# Revit family: Building-IEC309Connections-GEWISS-44IB-INTERLOCKED-SOCKET-OUTLETS_IP44_WITHOUT_BOTTOM
name_source: partatom
category: Apparecchi elettrici
revit_build: Autodesk Revit 2016 (Build: 20161004_0715(x64)
units: mm (PartAtom-declared; Revit-internal decimal feet)

## family parameters
Condiviso = No
Host = Muro
Mantenere orientamento annotazione = Sì
Numero OmniClass = 23.80.50.14
Punto di calcolo locali = No
Quota connettore circolare = Usa diametro
Sempre verticale = Sì
Taglio con vuoti quando caricato = No
Tipo di parte = Normale
Titolo OmniClass = Plug Connectors

## types (22) — shared parameters
Altezza da terra = 820 mm
Carico apparente = 0 VA
Catalogue = BUILDING
Catalogue Range = 44 IB
Classificazione carico = Altro
Electrocod = 2220
Frequency = 50/60 Hz
Glow Wire Test = 850 °C (active parts) - 650 °C (passive parts)
Glow wire test: = 850 °C (active parts) - 650 °C (passive parts)
IDF = e04837b6-ddbd-45f3-abac-050fc58771e5
IDT = ec1a1901-e242-435b-8cd0-c029da0151fc
IP degree = IP44
Immagine tipo = GW66110.jpg
Numero poli = 3
Operating temperature: = -25 +40 °C
Potenza = 500 V
Presa = GEWISS - NERO
Produttore = GEWISS S.p.A.
Protection = NO (SBF)
Rated frequency (Hz) = 50/60 Hz
SEO = Socket outlet
Shock resistance = IK08
Struttura = GEWISS - Grigio RAL - 7035
Technical sheet = https://www.gewiss.com
Thermo-pressure with ball = 125
Tipo simbolo = PRESAIND : 3P
Typology = Horizontal
URL = https://www.gewiss.com
Version file RFA = 18.0
Vetro = GEWISS - vetro
With back-mounting box = No
Working temperature = -25 ÷ +40 °C

## per-type parameters (varying)
| type | Colour | Colour: | Descrizione | EAN code | Modello | No. of poles | Number of poles | Rated current (A) | Rated current (In) | Rated voltage | Reference h |
| GW66103 - 16A 3P+N+E 110V H.INT.SOCK.O.N.B. 4H SBF | Yellow | Yellow | 16A 3P+N+E 110V H.INT.SOCK.O.N.B. 4H SBF | 8011564029095 | GW66103 | 3P+N+E | 3P+N+E | 16 | 16 | 100-130V | 4 |
| GW66112 - 32A 2P+E 110V H.INT.SOCK.O.N.B. 4H SBF | Yellow | Yellow | 32A 2P+E 110V H.INT.SOCK.O.N.B. 4H SBF | 8011564029187 | GW66112 | 2P+E | 2P+E | 32 | 32 | 100-130V | 4 |
| GW66122 - 32A 3P+N+E 500V H.INT.SOCK.O.N.B. 7H SBF | Black | Black | 32A 3P+N+E 500V H.INT.SOCK.O.N.B. 7H SBF | 8011564029286 | GW66122 | 3P+N+E | 3P+N+E | 32 | 32 | 480-500V | 7 |
| GW66117 - 32A 3P+N+E 230V H.INT.SOCK.O.N.B. 9H SBF | Blue | Blue | 32A 3P+N+E 230V H.INT.SOCK.O.N.B. 9H SBF | 8011564029231 | GW66117 | 3P+N+E | 3P+N+E | 32 | 32 | 200-250V | 9 |
| GW66110 - 16A 3P+E 500V H.INT.SOCK.O.N.B. 7H SBF | Black | Black | 16A 3P+E 500V H.INT.SOCK.O.N.B. 7H SBF | 8011564029163 | GW66110 | 3P+E | 3P+E | 16 | 16 | 480-500V | 7 |
| GW66121 - 32A 3P+E 500V H.INT.SOCK.O.N.B. 7H SBF | Black | Black | 32A 3P+E 500V H.INT.SOCK.O.N.B. 7H SBF | 8011564029279 | GW66121 | 3P+E | 3P+E | 32 | 32 | 480-500V | 7 |
| GW66120 - 32A 3P+N+E 400V H.INT.SOCK.O.N.B. 6H SBF | Red | Red | 32A 3P+N+E 400V H.INT.SOCK.O.N.B. 6H SBF | 8011564029262 | GW66120 | 3P+N+E | 3P+N+E | 32 | 32 | 380-415V | 6 |
| GW66106 - 16A 3P+N+E 230V H.INT.SOCK.O.N.B. 9H SBF | Blue | Blue | 16A 3P+N+E 230V H.INT.SOCK.O.N.B. 9H SBF | 8011564029125 | GW66106 | 3P+N+E | 3P+N+E | 16 | 16 | 200-250V | 9 |
| GW66104 - 16A 2P+E 230V H.INT.SOCK.O.N.B. 6H SBF | Blue | Blue | 16A 2P+E 230V H.INT.SOCK.O.N.B. 6H SBF | 8011564029101 | GW66104 | 2P+E | 2P+E | 16 | 16 | 200-250V | 6 |
| GW66107 - 16A 2P+E 400V H.INT.SOCK.O.N.B. 9H SBF | Red | Red | 16A 2P+E 400V H.INT.SOCK.O.N.B. 9H SBF | 8011564029132 | GW66107 | 2P+E | 2P+E | 16 | 16 | 380-415V | 9 |
| GW66101 - 16A 2P+E 110V H.INT.SOCK.O.N.B. 4H SBF | Yellow | Yellow | 16A 2P+E 110V H.INT.SOCK.O.N.B. 4H SBF | 8011564029071 | GW66101 | 2P+E | 2P+E | 16 | 16 | 100-130V | 4 |
| GW66116 - 32A 3P+E 230V H.INT.SOCK.O.N.B. 9H SBF | Blue | Blue | 32A 3P+E 230V H.INT.SOCK.O.N.B. 9H SBF | 8011564029224 | GW66116 | 3P+E | 3P+E | 32 | 32 | 200-250V | 9 |
| GW66119 - 32A 3P+E 400V H.INT.SOCK.O.N.B. 6H SBF | Red | Red | 32A 3P+E 400V H.INT.SOCK.O.N.B. 6H SBF | 8011564029255 | GW66119 | 3P+E | 3P+E | 32 | 32 | 380-415V | 6 |
| GW66109 - 16A 3P+N+E 400V H.INT.SOCK.O.N.B. 6H SBF | Red | Red | 16A 3P+N+E 400V H.INT.SOCK.O.N.B. 6H SBF | 8011564029156 | GW66109 | 3P+N+E | 3P+N+E | 16 | 16 | 380-415V | 6 |
| GW66113 - 32A 3P+E 110V H.INT.SOCK.O.N.B. 4H SBF | Yellow | Yellow | 32A 3P+E 110V H.INT.SOCK.O.N.B. 4H SBF | 8011564029194 | GW66113 | 3P+E | 3P+E | 32 | 32 | 100-130V | 4 |
| GW66105 - 16A 3P+E 230V H.INT.SOCK.O.N.B. 9H SBF | Blue | Blue | 16A 3P+E 230V H.INT.SOCK.O.N.B. 9H SBF | 8011564029118 | GW66105 | 3P+E | 3P+E | 16 | 16 | 200-250V | 9 |
| GW66115 - 32A 2P+E 230V H.INT.SOCK.O.N.B. 6H SBF | Blue | Blue | 32A 2P+E 230V H.INT.SOCK.O.N.B. 6H SBF | 8011564029217 | GW66115 | 2P+E | 2P+E | 32 | 32 | 200-250V | 6 |
| GW66114 - 32A 3P+N+E 110V H.INT.SOCK.O.N.B. 4H SBF | Yellow | Yellow | 32A 3P+N+E 110V H.INT.SOCK.O.N.B. 4H SBF | 8011564029200 | GW66114 | 3P+N+E | 3P+N+E | 32 | 32 | 100-130V | 4 |
| GW66102 - 16A 3P+E 110V H.INT.SOCK.O.N.B. 4H SBF | Yellow | Yellow | 16A 3P+E 110V H.INT.SOCK.O.N.B. 4H SBF | 8011564029088 | GW66102 | 3P+E | 3P+E | 16 | 16 | 100-130V | 4 |
| GW66118 - 32A 2P+E 400V H.INT.SOCK.O.N.B. 9H SBF | Red | Red | 32A 2P+E 400V H.INT.SOCK.O.N.B. 9H SBF | 8011564029248 | GW66118 | 2P+E | 2P+E | 32 | 32 | 380-415V | 9 |
| GW66108 - 16A 3P+E 400V H.INT.SOCK.O.N.B. 6H SBF | Red | Red | 16A 3P+E 400V H.INT.SOCK.O.N.B. 6H SBF | 8011564029149 | GW66108 | 3P+E | 3P+E | 16 | 16 | 380-415V | 6 |
| GW66111 - 16A 3P+N+E 500V H.INT.SOCK.O.N.B. 7H SBF | Black | Black | 16A 3P+N+E 500V H.INT.SOCK.O.N.B. 7H SBF | 8011564029170 | GW66111 | 3P+N+E | 3P+N+E | 16 | 16 | 480-500V | 7 |

note: source unit labels omitted for Thermo-pressure with ball — the stored unit's dimension contradicts the parameter name (converter mislabeling)

## geometry (parser evidence)
native form markers: Sweep x2
no freeform markers — native parametric forms only
